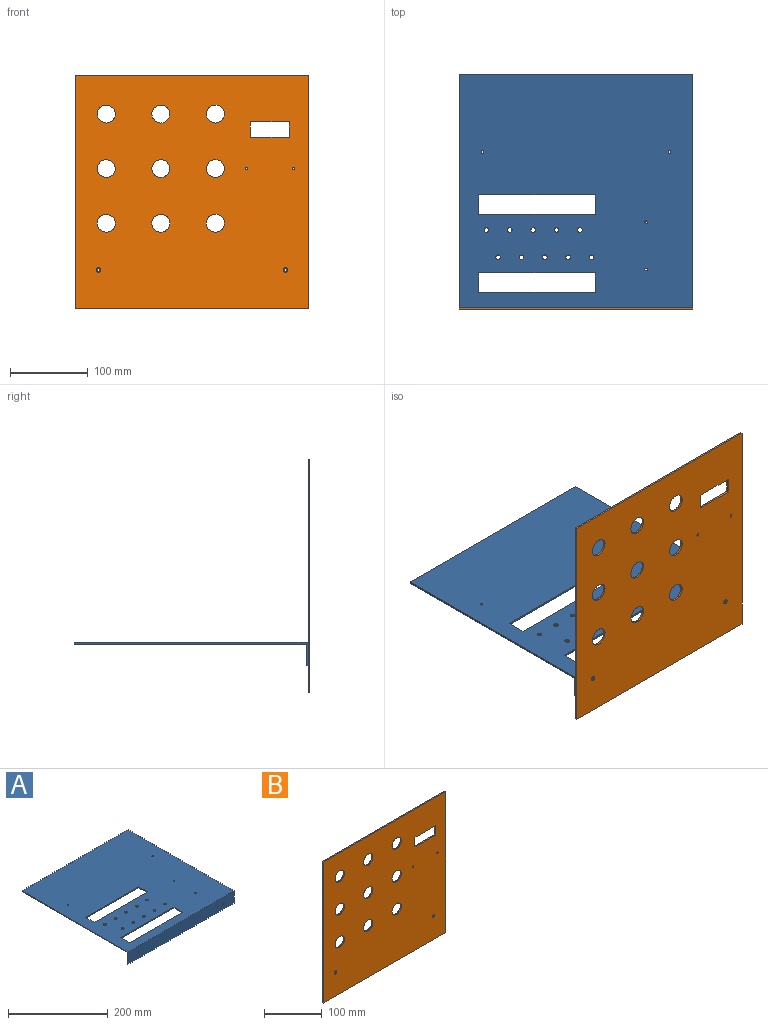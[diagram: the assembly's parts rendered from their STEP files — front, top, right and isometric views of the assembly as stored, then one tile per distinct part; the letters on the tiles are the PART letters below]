
ASSEMBLY  parts=2 mates=1
PART A: 32 faces, bbox 300x300x30 mm
  f0: plane 300x297.7mm, normal (0,0,-1), area 81493mm2, adj f3,f4,f5,f6,f8,f9,f10,f11
  f1: plane 300x300mm, normal (0,0,1), area 82183mm2, adj f2,f3,f4,f5,f8,f9,f10,f11
  f2: plane 300x30mm, normal (0,-1,0), area 8972.3mm2, adj f1,f3,f5,f7,f18,f19
  f3: plane 300x30mm, normal (1,0,0), area 753.7mm2, adj f0,f1,f2,f4,f6,f7
  f4: plane 300x2.3mm, normal (0,1,0), area 690mm2, adj f0,f1,f3,f5
  f5: plane 300x30mm, normal (-1,0,0), area 753.7mm2, adj f0,f1,f2,f4,f6,f7
  f6: plane 300x27.7mm, normal (0,1,0), area 8282.3mm2, adj f0,f3,f5,f7,f18,f19
  f7: plane 300x2.3mm, normal (0,0,-1), area 690mm2, adj f2,f3,f5,f6
  f8: plane 25x2.3mm, normal (1,0,0), area 57.5mm2, adj f0,f1,f9,f11
  f9: plane 150x2.3mm, normal (0,1,0), area 345mm2, adj f0,f1,f8,f10
  f10: plane 25x2.3mm, normal (-1,0,0), area 57.5mm2, adj f0,f1,f9,f11
  f11: plane 150x2.3mm, normal (0,-1,0), area 345mm2, adj f0,f1,f8,f10
  f12: plane 150x2.3mm, normal (0,-1,0), area 345mm2, adj f0,f1,f13,f15
  f13: plane 25x2.3mm, normal (1,0,0), area 57.5mm2, adj f0,f1,f12,f14
  f14: plane 150x2.3mm, normal (0,1,0), area 345mm2, adj f0,f1,f13,f15
  f15: plane 25x2.3mm, normal (-1,0,0), area 57.5mm2, adj f0,f1,f12,f14
  f16: cylinder r=1.65mm len=3.3mm, axis (0,0,1), area 23.8mm2, adj f0,f1
  f17: cylinder r=1.65mm len=3.3mm, axis (0,0,1), area 23.8mm2, adj f0,f1
  f18: cylinder r=2.1mm len=4.2mm, axis (0,-1,0), area 30.3mm2, adj f2,f6
  f19: cylinder r=2.1mm len=4.2mm, axis (0,-1,0), area 30.3mm2, adj f2,f6
  f20: cylinder r=3mm len=6mm, axis (0,0,1), area 43.4mm2, adj f0,f1
  f21: cylinder r=3mm len=6mm, axis (0,0,1), area 43.4mm2, adj f0,f1
  f22: cylinder r=3mm len=6mm, axis (0,0,1), area 43.4mm2, adj f0,f1
  f23: cylinder r=3mm len=6mm, axis (0,0,1), area 43.4mm2, adj f0,f1
  f24: cylinder r=3mm len=6mm, axis (0,0,1), area 43.4mm2, adj f0,f1
  f25: cylinder r=3mm len=6mm, axis (0,0,1), area 43.4mm2, adj f0,f1
  f26: cylinder r=3mm len=6mm, axis (0,0,1), area 43.4mm2, adj f0,f1
  f27: cylinder r=3mm len=6mm, axis (0,0,1), area 43.4mm2, adj f0,f1
  f28: cylinder r=3mm len=6mm, axis (0,0,1), area 43.4mm2, adj f0,f1
  f29: cylinder r=3mm len=6mm, axis (0,0,1), area 43.4mm2, adj f0,f1
  f30: cylinder r=1.65mm len=3.3mm, axis (0,0,1), area 23.8mm2, adj f0,f1
  f31: cylinder r=1.65mm len=3.3mm, axis (0,0,1), area 23.8mm2, adj f0,f1
PART B: 23 faces, bbox 300x2.3x300 mm
  f0: plane 300x300mm, normal (0,-1,0), area 85187.1mm2, adj f2,f3,f4,f5,f6,f7,f8,f9
  f1: plane 300x300mm, normal (0,1,0), area 85187.1mm2, adj f2,f3,f4,f5,f6,f7,f8,f9
  f2: plane 300x2.3mm, normal (0,0,-1), area 690mm2, adj f0,f1,f3,f5
  f3: plane 300x2.3mm, normal (1,0,0), area 690mm2, adj f0,f1,f2,f4
  f4: plane 300x2.3mm, normal (0,0,1), area 690mm2, adj f0,f1,f3,f5
  f5: plane 300x2.3mm, normal (-1,0,0), area 690mm2, adj f0,f1,f2,f4
  f6: cylinder r=3mm len=6mm, axis (0,-1,0), area 43.4mm2, adj f0,f1
  f7: cylinder r=3mm len=6mm, axis (0,-1,0), area 43.4mm2, adj f0,f1
  f8: cylinder r=11.5mm len=23mm, axis (0,-1,0), area 166.2mm2, adj f0,f1
  f9: cylinder r=11.5mm len=23mm, axis (0,-1,0), area 166.2mm2, adj f0,f1
  f10: cylinder r=11.5mm len=23mm, axis (0,-1,0), area 166.2mm2, adj f0,f1
  f11: cylinder r=11.5mm len=23mm, axis (0,-1,0), area 166.2mm2, adj f0,f1
  f12: cylinder r=11.5mm len=23mm, axis (0,-1,0), area 166.2mm2, adj f0,f1
  f13: cylinder r=11.5mm len=23mm, axis (0,-1,0), area 166.2mm2, adj f0,f1
  f14: cylinder r=11.5mm len=23mm, axis (0,-1,0), area 166.2mm2, adj f0,f1
  f15: cylinder r=11.5mm len=23mm, axis (0,-1,0), area 166.2mm2, adj f0,f1
  f16: cylinder r=11.5mm len=23mm, axis (0,-1,0), area 166.2mm2, adj f0,f1
  f17: cylinder r=1.65mm len=3.3mm, axis (0,-1,0), area 23.8mm2, adj f0,f1
  f18: cylinder r=1.65mm len=3.3mm, axis (0,-1,0), area 23.8mm2, adj f0,f1
  f19: plane 50x2.3mm, normal (0,0,1), area 115mm2, adj f0,f1,f20,f22
  f20: plane 20x2.3mm, normal (-1,0,0), area 46mm2, adj f0,f1,f19,f21
  f21: plane 50x2.3mm, normal (0,0,-1), area 115mm2, adj f0,f1,f20,f22
  f22: plane 20x2.3mm, normal (1,0,0), area 46mm2, adj f0,f1,f19,f21
PLACE A t=(-58.38,-51.61,-30.67)mm
PLACE B t=(-60.8,-201.61,54.33)mm
MATE fastened B.f6 <-> A.f18  axis (0,1,0) through (61.62,-201.61,-45.67)mm
